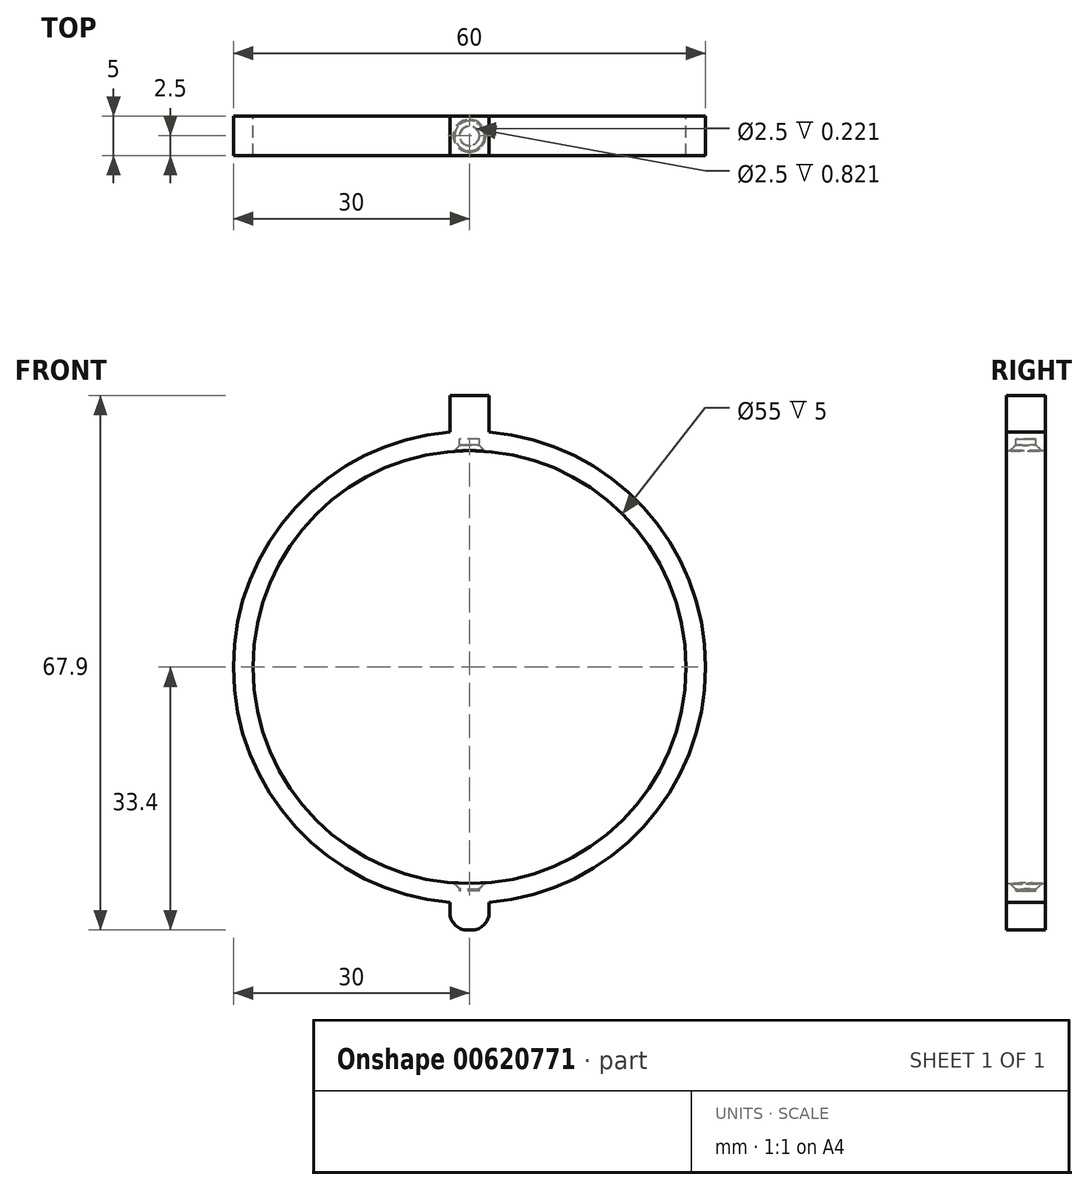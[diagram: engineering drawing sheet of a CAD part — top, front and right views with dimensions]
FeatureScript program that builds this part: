
annotation { "Feature Type Name" : "Feature", "Feature Type Description" : "" }
export const myFeature = defineFeature(function(context is Context, id is Id, definition is map)
    precondition{}
    {
        {
            var Q0;
            Q0=qCreatedBy(makeId("Front.planeOp"),FACE);
            var sketch = newSketch(context, id + "F0", { "sketchPlane" : qUnion([Q0])});
            skCircle(sketch, "E0", {"center": v(0, 0) * mm, "radius": 30 * mm});
            skCircle(sketch, "E1", {"center": v(0, 0) * mm, "radius": 27.5 * mm});
            skSolve(sketch);
        }
        {
            var Q0;
            Q0 = qSketchRegion(id + "F0", true);
            extrude(context, id + "F1", {"entities" : qUnion([Q0]), "depth" : 5 * mm, "offsetDistance" : 25 * mm});
        }
        {
            var Q0;
            Q0=qCreatedBy(makeId("Top.planeOp"),FACE);
            var sketch = newSketch(context, id + "F2", { "sketchPlane" : qUnion([Q0])});
            skCircle(sketch, "E2", {"center": v(0, -2.5) * mm, "radius": 1.25 * mm});
            skSolve(sketch);
        }
        {
            var Q0;
            Q0 = qSketchRegion(id + "F2", true);
            extrude(context, id + "F3", {"entities" : qUnion([Q0]), "operationType" : NewBodyOperationType.REMOVE, "endBound" : BoundingType.SYMMETRIC, "oppositeDirection" : true, "depth" : 58 * mm, "offsetDistance" : 25 * mm});
        }
        {
            var Q0;
            Q0=makeQuery(id+"F3.boolean.opBoolean","INTERSECT",EDGE,{"disambiguationData":[OD(0.0)],"derivedFrom":[makeQuery(id+"F1.opExtrude","SWEPT_FACE",FACE,{"disambiguationData":[OSD([sQuery(id+"F0.wireOp",EDGE,"E1")])]}),makeQuery(id+"F3.opExtrude","SWEPT_FACE",FACE,{"disambiguationData":[OSD([sQuery(id+"F2.wireOp",EDGE,"E2")])]})]});
            chamfer(context, id + "F4", {"entities" : qUnion([Q0]), "width" : .75 * mm, "tangentPropagation" : true});
        }
        {
            var Q0;
            Q0=makeQuery(id+"F3.boolean.opBoolean","INTERSECT",EDGE,{"disambiguationData":[OD(1.0)],"derivedFrom":[makeQuery(id+"F1.opExtrude","SWEPT_FACE",FACE,{"disambiguationData":[OSD([sQuery(id+"F0.wireOp",EDGE,"E1")])]}),makeQuery(id+"F3.opExtrude","SWEPT_FACE",FACE,{"disambiguationData":[OSD([sQuery(id+"F2.wireOp",EDGE,"E2")])]})]});
            chamfer(context, id + "F5", {"entities" : qUnion([Q0]), "width" : .75 * mm, "tangentPropagation" : true});
        }
        {
            var Q0;
            {var subQ0=makeQuery(id+"F1.opExtrude","SWEPT_FACE",FACE,{"disambiguationData":[OSD([sQuery(id+"F0.wireOp",EDGE,"E1")])]});Q0=makeQuery(id+"F4.opChamfer","BLEND_EDGE",EDGE,{"blendedFrom":[makeQuery(id+"F3.boolean.opBoolean","INTERSECT",EDGE,{"disambiguationData":[OD(0.0)],"derivedFrom":[subQ0,makeQuery(id+"F3.opExtrude","SWEPT_FACE",FACE,{"disambiguationData":[OSD([sQuery(id+"F2.wireOp",EDGE,"E2")])]})]}),subQ0],"blendedInto":[subQ0]});}
            fillet(context, id + "F6", {"entities" : qUnion([Q0]), "radius" : .25 * mm, "tangentPropagation" : true, "allowEdgeOverflow" : false});
        }
        {
            var Q0;
            {var subQ0=makeQuery(id+"F1.opExtrude","SWEPT_FACE",FACE,{"disambiguationData":[OSD([sQuery(id+"F0.wireOp",EDGE,"E1")])]});Q0=makeQuery(id+"F5.opChamfer","BLEND_EDGE",EDGE,{"blendedFrom":[makeQuery(id+"F3.boolean.opBoolean","INTERSECT",EDGE,{"disambiguationData":[OD(1.0)],"derivedFrom":[subQ0,makeQuery(id+"F3.opExtrude","SWEPT_FACE",FACE,{"disambiguationData":[OSD([sQuery(id+"F2.wireOp",EDGE,"E2")])]})]}),subQ0],"blendedInto":[subQ0]});}
            fillet(context, id + "F7", {"entities" : qUnion([Q0]), "radius" : .25 * mm, "tangentPropagation" : true, "allowEdgeOverflow" : false});
        }
        {
            var Q0;
            Q0=qCreatedBy(makeId("Top.planeOp"),FACE);
            cPlane(context, id + "F8", {"entities" : qUnion([Q0]), "cplaneType" : CPlaneType.OFFSET, "offset" : 29.5 * mm, "width" : 150 * mm, "height" : 150 * mm});
        }
        {
            var Q0;
            Q0=qCreatedBy(id+"F8.planeOp",FACE);
            var sketch = newSketch(context, id + "F9", { "sketchPlane" : qUnion([Q0])});
            skLineSegment(sketch, "E3.bottom", {"start": v(-2.5, 0) * mm, "end": v(2.5, 0) * mm});
            skLineSegment(sketch, "E3.top", {"start": v(-2.5, -5.57) * mm, "end": v(2.5, -5.57) * mm});
            skLineSegment(sketch, "E3.left", {"start": v(-2.5, 0) * mm, "end": v(-2.5, -5.57) * mm});
            skLineSegment(sketch, "E3.right", {"start": v(2.5, 0) * mm, "end": v(2.5, -5.57) * mm});
            skPoint(sketch, "E3.middle", {"position": v(0, -2.79) * mm});
            skSolve(sketch);
        }
        {
            var Q0;
            Q0 = qSketchRegion(id + "F9", true);
            extrude(context, id + "F10", {"entities" : qUnion([Q0]), "operationType" : NewBodyOperationType.ADD, "depth" : 5 * mm, "offsetDistance" : 25 * mm});
        }
        {
            var Q0;
            Q0=makeQuery(id+"F10.opExtrude","CAP_FACE",FACE,{"disambiguationData":[OSD([sQuery(id+"F9.wireOp",EDGE,"E3.bottom"),sQuery(id+"F9.wireOp",EDGE,"E3.top"),sQuery(id+"F9.wireOp",EDGE,"E3.left"),sQuery(id+"F9.wireOp",EDGE,"E3.right")])],"isStart":false});
            var sketch = newSketch(context, id + "F11", { "sketchPlane" : qUnion([Q0])});
            skLineSegment(sketch, "E4", {"start": v(30, 0) * mm, "end": v(30, -5) * mm});
            skLineSegment(sketch, "E5", {"start": v(-30, -5) * mm, "end": v(-30, 0) * mm});
            skLineSegment(sketch, "E6.top", {"start": v(-2.5, -5) * mm, "end": v(2.5, -5) * mm});
            skLineSegment(sketch, "E7.bottom", {"start": v(-2.5, -5) * mm, "end": v(2.51, -5) * mm});
            skLineSegment(sketch, "E7.top", {"start": v(-2.5, -7.2) * mm, "end": v(2.51, -7.2) * mm});
            skLineSegment(sketch, "E7.left", {"start": v(-2.5, -5) * mm, "end": v(-2.5, -7.2) * mm});
            skLineSegment(sketch, "E7.right", {"start": v(2.51, -5) * mm, "end": v(2.51, -7.2) * mm});
            skSolve(sketch);
        }
        {
            var Q0;
            {var subQ5=makeQuery(id+"F10.opExtrude","CAP_EDGE",EDGE,{"disambiguationData":[OSD([sQuery(id+"F9.wireOp",EDGE,"E3.top")])],"isStart":false});Q0=makeQuery(id+"F11.imprint","IMPRINT",FACE,{"disambiguationData":[TD([[makeQuery(id+"F11.imprint","IMPRINT",EDGE,{"derivedFrom":subQ5}),1.0]])]});}
            extrude(context, id + "F12", {"entities" : qUnion([Q0]), "operationType" : NewBodyOperationType.REMOVE, "oppositeDirection" : true, "depth" : 25 * mm, "offsetDistance" : 25 * mm});
        }
        {
            var Q0;
            Q0=qCreatedBy(makeId("Top.planeOp"),FACE);
            cPlane(context, id + "F13", {"entities" : qUnion([Q0]), "cplaneType" : CPlaneType.OFFSET, "offset" : 28.4 * mm, "oppositeDirection" : true, "width" : 150 * mm, "height" : 150 * mm});
        }
        {
            var Q0;
            Q0=qCreatedBy(id+"F13.planeOp",FACE);
            var sketch = newSketch(context, id + "F14", { "sketchPlane" : qUnion([Q0])});
            skLineSegment(sketch, "E8.bottom", {"start": v(-2.5, -5) * mm, "end": v(2.5, -5) * mm});
            skLineSegment(sketch, "E8.top", {"start": v(-2.5, 0) * mm, "end": v(2.5, 0) * mm});
            skLineSegment(sketch, "E8.left", {"start": v(-2.5, -5) * mm, "end": v(-2.5, 0) * mm});
            skLineSegment(sketch, "E8.right", {"start": v(2.5, -5) * mm, "end": v(2.5, 0) * mm});
            skPoint(sketch, "E8.middle", {"position": v(0, -2.5) * mm});
            skSolve(sketch);
        }
        {
            var Q0;
            Q0 = qSketchRegion(id + "F14", true);
            extrude(context, id + "F15", {"entities" : qUnion([Q0]), "operationType" : NewBodyOperationType.ADD, "oppositeDirection" : true, "depth" : 5 * mm, "offsetDistance" : 25 * mm});
        }
        {
            var Q0;
            Q0=makeQuery(id+"F15.opExtrude","CAP_EDGE",EDGE,{"disambiguationData":[OSD([sQuery(id+"F14.wireOp",EDGE,"E8.left")])],"isStart":false});
            var Q1;
            Q1=makeQuery(id+"F15.opExtrude","CAP_EDGE",EDGE,{"disambiguationData":[OSD([sQuery(id+"F14.wireOp",EDGE,"E8.right")])],"isStart":false});
            fillet(context, id + "F16", {"entities" : qUnion([Q0, Q1]), "radius" : 2.25 * mm, "tangentPropagation" : true, "allowEdgeOverflow" : false});
        }
    });
